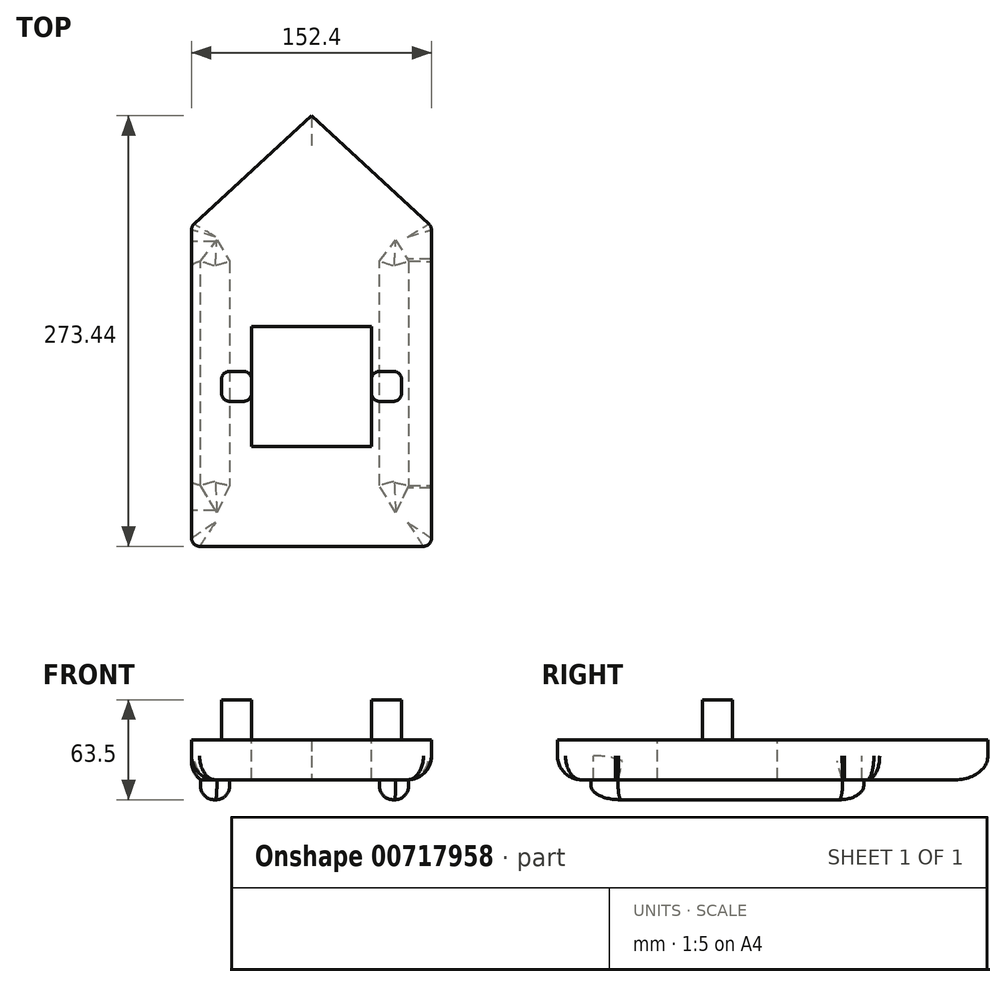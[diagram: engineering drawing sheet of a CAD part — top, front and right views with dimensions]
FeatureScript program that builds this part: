
annotation { "Feature Type Name" : "Feature", "Feature Type Description" : "" }
export const myFeature = defineFeature(function(context is Context, id is Id, definition is map)
    precondition{}
    {
        {
            var Q0;
            Q0=qCreatedBy(makeId("Top.planeOp"),FACE);
            var sketch = newSketch(context, id + "F0", { "sketchPlane" : qUnion([Q0])});
            skLineSegment(sketch, "E0.bottom", {"start": v(-152.4, 91.7) * mm, "end": v(0, 91.7) * mm});
            skLineSegment(sketch, "E0.top", {"start": v(-152.4, -111.5) * mm, "end": v(0, -111.5) * mm});
            skLineSegment(sketch, "E0.left", {"start": v(-152.4, 91.7) * mm, "end": v(-152.4, -111.5) * mm});
            skLineSegment(sketch, "E0.right", {"start": v(0, 91.7) * mm, "end": v(0, -111.5) * mm});
            skLineSegment(sketch, "E1", {"start": v(-76.2, 161.94) * mm, "end": v(-152.4, 91.7) * mm});
            skPoint(sketch, "E1.startSnap0", {"position": v(-76.2, 91.7) * mm});
            skLineSegment(sketch, "E2", {"start": v(-76.2, 161.94) * mm, "end": v(0, 91.7) * mm});
            skSolve(sketch);
        }
        {
            var Q0;
            Q0=qSketchRegion(id+"F0",true);
            extrude(context, id + "F1", {"entities" : qUnion([Q0]), "depth" : 25.4 * mm, "offsetDistance" : 25.4 * mm});
        }
        {
            var Q0;
            Q0=makeQuery(id+"F1.opExtrude","CAP_FACE",FACE,{"disambiguationData":[OSD([sQuery(id+"F0.wireOp",EDGE,"E0.bottom"),sQuery(id+"F0.wireOp",EDGE,"E0.top"),sQuery(id+"F0.wireOp",EDGE,"E0.left"),sQuery(id+"F0.wireOp",EDGE,"E0.right")])],"isStart":false});
            var sketch = newSketch(context, id + "F2", { "sketchPlane" : qUnion([Q0])});
            skLineSegment(sketch, "E3.bottom", {"start": v(-114.3, 28.2) * mm, "end": v(-38.1, 28.2) * mm});
            skLineSegment(sketch, "E3.top", {"start": v(-114.3, -48) * mm, "end": v(-38.1, -48) * mm});
            skLineSegment(sketch, "E3.left", {"start": v(-114.3, 28.2) * mm, "end": v(-114.3, -48) * mm});
            skLineSegment(sketch, "E3.right", {"start": v(-38.1, 28.2) * mm, "end": v(-38.1, -48) * mm});
            skSolve(sketch);
        }
        {
            var Q0;
            Q0=qSketchRegion(id+"F2",true);
            extrude(context, id + "F3", {"entities" : qUnion([Q0]), "operationType" : NewBodyOperationType.REMOVE, "oppositeDirection" : true, "depth" : 76.2 * mm, "offsetDistance" : 25.4 * mm});
        }
        {
            var Q0;
            Q0=makeQuery(id+"F1.opExtrude","CAP_FACE",FACE,{"disambiguationData":[OSD([sQuery(id+"F0.wireOp",EDGE,"E0.bottom"),sQuery(id+"F0.wireOp",EDGE,"E0.top"),sQuery(id+"F0.wireOp",EDGE,"E0.left"),sQuery(id+"F0.wireOp",EDGE,"E0.right")])],"isStart":false});
            var sketch = newSketch(context, id + "F4", { "sketchPlane" : qUnion([Q0])});
            skLineSegment(sketch, "E4.bottom", {"start": v(-114.3, -0.38) * mm, "end": v(-133.35, -0.38) * mm});
            skLineSegment(sketch, "E4.top", {"start": v(-114.3, -19.43) * mm, "end": v(-133.35, -19.43) * mm});
            skLineSegment(sketch, "E4.left", {"start": v(-114.3, -0.38) * mm, "end": v(-114.3, -19.43) * mm});
            skLineSegment(sketch, "E4.right", {"start": v(-133.35, -0.38) * mm, "end": v(-133.35, -19.43) * mm});
            skLineSegment(sketch, "E5.bottom", {"start": v(-38.1, -0.38) * mm, "end": v(-19.05, -0.38) * mm});
            skLineSegment(sketch, "E5.top", {"start": v(-38.1, -19.43) * mm, "end": v(-19.05, -19.43) * mm});
            skLineSegment(sketch, "E5.left", {"start": v(-38.1, -0.38) * mm, "end": v(-38.1, -19.43) * mm});
            skLineSegment(sketch, "E5.right", {"start": v(-19.05, -0.38) * mm, "end": v(-19.05, -19.43) * mm});
            skSolve(sketch);
        }
        {
            var Q0;
            Q0=qSketchRegion(id+"F4",true);
            extrude(context, id + "F5", {"entities" : qUnion([Q0]), "operationType" : NewBodyOperationType.ADD, "depth" : 25.4 * mm, "offsetDistance" : 25.4 * mm});
        }
        {
            var Q0;
            Q0=makeQuery(id+"F1.opExtrude","SWEPT_EDGE",EDGE,{"disambiguationData":[OSD([sQuery(id+"F0.wireOp",EDGE,"E0.bottom"),sQuery(id+"F0.wireOp",EDGE,"E0.right")])]});
            var Q1;
            Q1=makeQuery(id+"F1.opExtrude","SWEPT_EDGE",EDGE,{"disambiguationData":[OSD([sQuery(id+"F0.wireOp",EDGE,"E0.bottom"),sQuery(id+"F0.wireOp",EDGE,"E0.left")])]});
            fillet(context, id + "F6", {"entities" : qUnion([Q0, Q1]), "radius" : 5.08 * mm, "tangentPropagation" : true, "allowEdgeOverflow" : false});
        }
        {
            var Q0;
            Q0=makeQuery(id+"F1.opExtrude","SWEPT_EDGE",EDGE,{"disambiguationData":[OSD([sQuery(id+"F0.wireOp",EDGE,"E0.top"),sQuery(id+"F0.wireOp",EDGE,"E0.right")])]});
            var Q1;
            Q1=makeQuery(id+"F1.opExtrude","SWEPT_EDGE",EDGE,{"disambiguationData":[OSD([sQuery(id+"F0.wireOp",EDGE,"E0.top"),sQuery(id+"F0.wireOp",EDGE,"E0.left")])]});
            fillet(context, id + "F7", {"entities" : qUnion([Q0, Q1]), "radius" : 5.08 * mm, "tangentPropagation" : true, "allowEdgeOverflow" : false});
        }
        {
            var Q0;
            Q0=makeQuery(id+"F5.opExtrude","SWEPT_EDGE",EDGE,{"disambiguationData":[OSD([sQuery(id+"F2.wireOp",EDGE,"E3.left"),sQuery(id+"F4.wireOp",EDGE,"E4.bottom"),sQuery(id+"F4.wireOp",EDGE,"E4.left")])]});
            var Q1;
            Q1=makeQuery(id+"F5.opExtrude","SWEPT_EDGE",EDGE,{"disambiguationData":[OSD([sQuery(id+"F2.wireOp",EDGE,"E3.left"),sQuery(id+"F4.wireOp",EDGE,"E4.top"),sQuery(id+"F4.wireOp",EDGE,"E4.left")])]});
            var Q2;
            Q2=makeQuery(id+"F5.opExtrude","SWEPT_EDGE",EDGE,{"disambiguationData":[OSD([sQuery(id+"F4.wireOp",EDGE,"E5.bottom"),sQuery(id+"F4.wireOp",EDGE,"E5.right")])]});
            var Q3;
            Q3=makeQuery(id+"F5.opExtrude","SWEPT_EDGE",EDGE,{"disambiguationData":[OSD([sQuery(id+"F4.wireOp",EDGE,"E5.top"),sQuery(id+"F4.wireOp",EDGE,"E5.right")])]});
            var Q4;
            Q4=makeQuery(id+"F5.opExtrude","SWEPT_EDGE",EDGE,{"disambiguationData":[OSD([sQuery(id+"F2.wireOp",EDGE,"E3.right"),sQuery(id+"F4.wireOp",EDGE,"E5.bottom"),sQuery(id+"F4.wireOp",EDGE,"E5.left")])]});
            var Q5;
            Q5=makeQuery(id+"F5.opExtrude","SWEPT_EDGE",EDGE,{"disambiguationData":[OSD([sQuery(id+"F2.wireOp",EDGE,"E3.right"),sQuery(id+"F4.wireOp",EDGE,"E5.top"),sQuery(id+"F4.wireOp",EDGE,"E5.left")])]});
            var Q6;
            Q6=makeQuery(id+"F5.opExtrude","SWEPT_EDGE",EDGE,{"disambiguationData":[OSD([sQuery(id+"F4.wireOp",EDGE,"E4.bottom"),sQuery(id+"F4.wireOp",EDGE,"E4.right")])]});
            var Q7;
            Q7=makeQuery(id+"F5.opExtrude","SWEPT_EDGE",EDGE,{"disambiguationData":[OSD([sQuery(id+"F4.wireOp",EDGE,"E4.top"),sQuery(id+"F4.wireOp",EDGE,"E4.right")])]});
            fillet(context, id + "F8", {"entities" : qUnion([Q0, Q1, Q2, Q3, Q4, Q5, Q6, Q7]), "radius" : 5.08 * mm, "tangentPropagation" : true, "allowEdgeOverflow" : false});
        }
        {
            var Q0;
            Q0=qCreatedBy(makeId("Top.planeOp"),FACE);
            var sketch = newSketch(context, id + "F9", { "sketchPlane" : qUnion([Q0])});
            skLineSegment(sketch, "E6", {"start": v(-22.69, -90.13) * mm, "end": v(-33.13, -72.93) * mm});
            skLineSegment(sketch, "E7", {"start": v(-33.13, -72.93) * mm, "end": v(-33.13, 69.54) * mm});
            skLineSegment(sketch, "E8", {"start": v(-33.13, 69.54) * mm, "end": v(-22.69, 83.05) * mm});
            skLineSegment(sketch, "E9", {"start": v(-22.69, 83.05) * mm, "end": v(-14.48, 69.54) * mm});
            skLineSegment(sketch, "E10", {"start": v(-14.48, 69.54) * mm, "end": v(-14.48, -72.93) * mm});
            skLineSegment(sketch, "E11", {"start": v(-14.48, -72.93) * mm, "end": v(-22.69, -90.13) * mm});
            skLineSegment(sketch, "E12", {"start": v(-136.3, 83.05) * mm, "end": v(-128.1, 69.54) * mm});
            skLineSegment(sketch, "E13", {"start": v(-128.1, 69.54) * mm, "end": v(-128.1, -72.93) * mm});
            skLineSegment(sketch, "E14", {"start": v(-128.1, -72.93) * mm, "end": v(-136.3, -90.13) * mm});
            skLineSegment(sketch, "E15", {"start": v(-136.3, -90.13) * mm, "end": v(-146.74, -72.93) * mm});
            skLineSegment(sketch, "E16", {"start": v(-146.74, -72.93) * mm, "end": v(-146.74, 69.54) * mm});
            skLineSegment(sketch, "E17", {"start": v(-146.74, 69.54) * mm, "end": v(-136.3, 83.05) * mm});
            skSolve(sketch);
        }
        {
            var Q0;
            Q0=qSketchRegion(id+"F9",true);
            extrude(context, id + "F10", {"entities" : qUnion([Q0]), "operationType" : NewBodyOperationType.ADD, "oppositeDirection" : true, "depth" : 12.7 * mm, "offsetDistance" : 25.4 * mm});
        }
        {
            var Q0;
            Q0=makeQuery(id+"F10.opExtrude","CAP_FACE",FACE,{"disambiguationData":[OSD([sQuery(id+"F9.wireOp",EDGE,"E6"),sQuery(id+"F9.wireOp",EDGE,"E7"),sQuery(id+"F9.wireOp",EDGE,"E8"),sQuery(id+"F9.wireOp",EDGE,"E9"),sQuery(id+"F9.wireOp",EDGE,"E10"),sQuery(id+"F9.wireOp",EDGE,"E11")])],"isStart":false});
            var Q1;
            Q1=makeQuery(id+"F10.opExtrude","CAP_FACE",FACE,{"disambiguationData":[OSD([sQuery(id+"F9.wireOp",EDGE,"E12"),sQuery(id+"F9.wireOp",EDGE,"E13"),sQuery(id+"F9.wireOp",EDGE,"E14"),sQuery(id+"F9.wireOp",EDGE,"E15"),sQuery(id+"F9.wireOp",EDGE,"E16"),sQuery(id+"F9.wireOp",EDGE,"E17")])],"isStart":false});
            fillet(context, id + "F11", {"entities" : qUnion([Q0, Q1]), "radius" : 8.9 * mm, "tangentPropagation" : true, "allowEdgeOverflow" : false});
        }
        {
            var Q0;
            Q0=makeQuery(id+"F1.opExtrude","CAP_EDGE",EDGE,{"disambiguationData":[OSD([sQuery(id+"F0.wireOp",EDGE,"E2")])],"isStart":true});
            fillet(context, id + "F12", {"entities" : qUnion([Q0]), "radius" : 15.24 * mm, "tangentPropagation" : true, "allowEdgeOverflow" : false});
        }
    });
